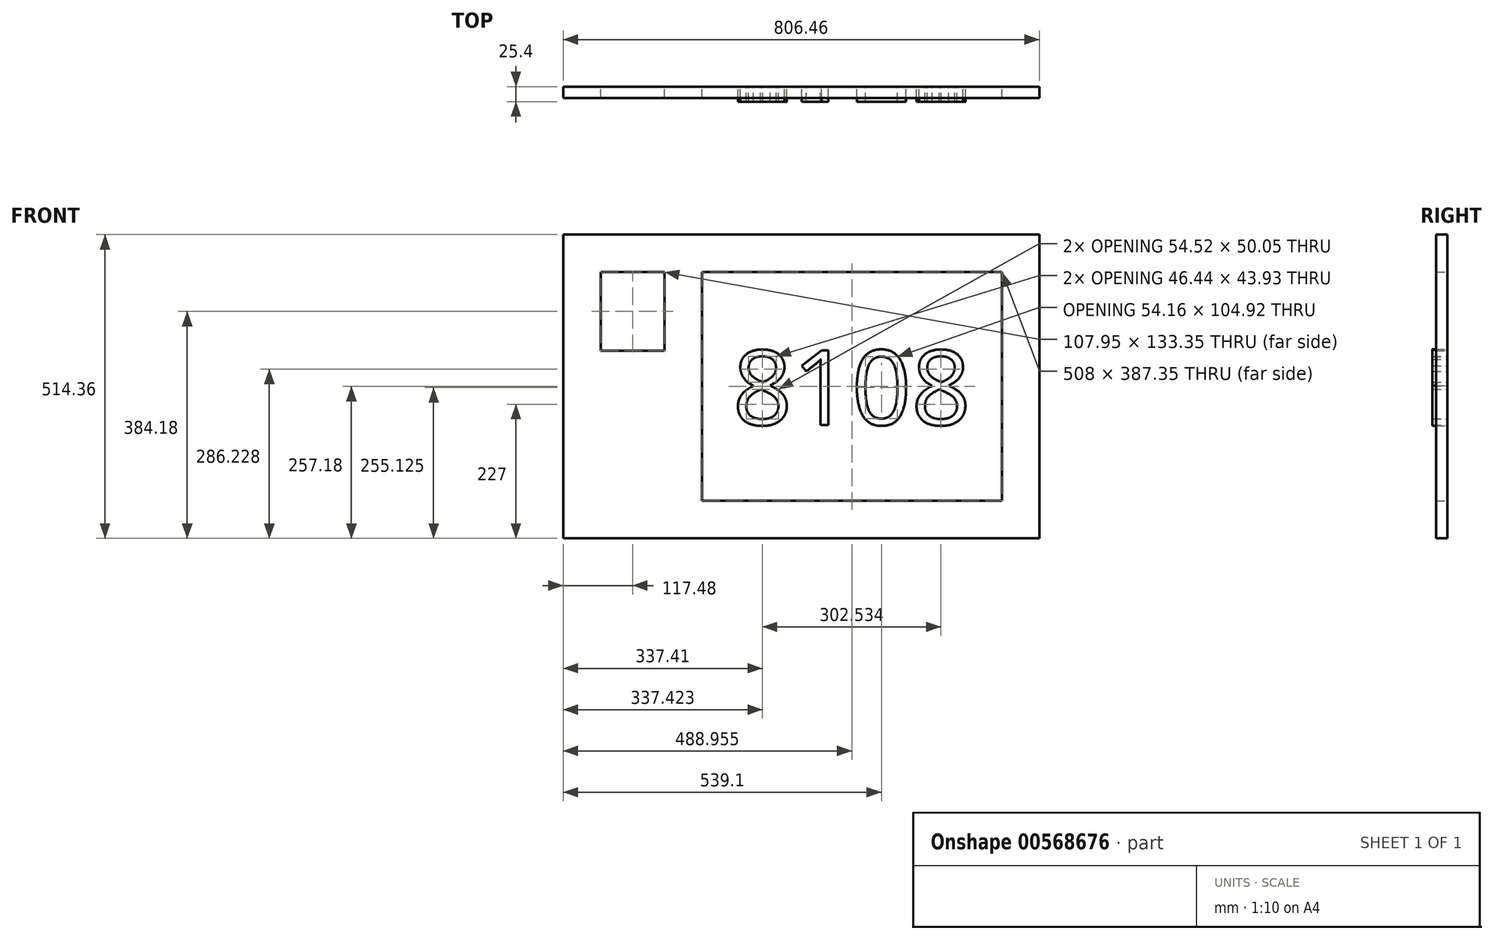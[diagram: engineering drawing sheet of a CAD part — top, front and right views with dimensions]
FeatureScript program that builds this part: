
annotation { "Feature Type Name" : "Feature", "Feature Type Description" : "" }
export const myFeature = defineFeature(function(context is Context, id is Id, definition is map)
    precondition{}
    {
        {
            var Q0;
            Q0=qCreatedBy(makeId("Front.planeOp"),FACE);
            var sketch = newSketch(context, id + "F0", { "sketchPlane" : qUnion([Q0])});
            skLineSegment(sketch, "E0.bottom", {"start": v(339.73, 193.68) * mm, "end": v(-339.73, 193.67) * mm});
            skLineSegment(sketch, "E0.top", {"start": v(339.73, -193.67) * mm, "end": v(-339.73, -193.68) * mm});
            skLineSegment(sketch, "E0.left", {"start": v(339.73, 193.68) * mm, "end": v(339.73, -193.67) * mm});
            skLineSegment(sketch, "E0.right", {"start": v(-339.73, 193.67) * mm, "end": v(-339.73, -193.68) * mm});
            skPoint(sketch, "E0.middle", {"position": v(0, 0) * mm});
            skLineSegment(sketch, "E1.0", {"start": v(403.23, 257.18) * mm, "end": v(403.23, -257.17) * mm});
            skLineSegment(sketch, "E1.1", {"start": v(403.23, 257.18) * mm, "end": v(-403.23, 257.17) * mm});
            skLineSegment(sketch, "E1.2", {"start": v(-403.23, 257.17) * mm, "end": v(-403.23, -257.18) * mm});
            skLineSegment(sketch, "E1.3", {"start": v(403.23, -257.17) * mm, "end": v(-403.23, -257.18) * mm});
            skLineSegment(sketch, "E2", {"start": v(-403.23, 257.17) * mm, "end": v(-339.73, 193.67) * mm});
            skLineSegment(sketch, "E3", {"start": v(403.23, 257.18) * mm, "end": v(339.73, 193.68) * mm});
            skLineSegment(sketch, "E4", {"start": v(339.73, -193.67) * mm, "end": v(403.23, -257.17) * mm});
            skLineSegment(sketch, "E5", {"start": v(-339.73, -193.68) * mm, "end": v(-403.23, -257.18) * mm});
            skLineSegment(sketch, "E6", {"start": v(-231.78, 193.67) * mm, "end": v(-231.77, -193.68) * mm});
            skLineSegment(sketch, "E7", {"start": v(-168.28, 193.67) * mm, "end": v(-168.28, -193.68) * mm});
            skLineSegment(sketch, "E8", {"start": v(-339.73, -3.18) * mm, "end": v(-231.78, -3.18) * mm});
            skLineSegment(sketch, "E9", {"start": v(-339.73, -130.18) * mm, "end": v(-231.77, -130.18) * mm});
            skLineSegment(sketch, "E10", {"start": v(-339.73, 60.32) * mm, "end": v(-231.78, 60.32) * mm});
            skText(sketch, "E11", { "text": "8108", "fontName": "OpenSans-Regular.ttf"});
            skLineSegment(sketch, "E12", {"start": v(-339.73, -66.68) * mm, "end": v(-231.78, -66.67) * mm});
            const initialGuessF0  = {"E11": [-0.11616, -0.0651, 1, 0, 0.127]};
            skSetInitialGuess(sketch, initialGuessF0);
            skSolve(sketch);
        }
        {
            var Q0;
            Q0=makeQuery(id+"F0.imprint","IMPRINT",FACE,{"disambiguationData":[TD([[makeQuery(id+"F0.imprint","IMPRINT",EDGE,{"derivedFrom":sQuery(id+"F0.wireOp",EDGE,"E1.2")}),1.0]])]});
            var Q1;
            Q1=makeQuery(id+"F0.imprint","IMPRINT",FACE,{"disambiguationData":[TD([[makeQuery(id+"F0.imprint","IMPRINT",EDGE,{"derivedFrom":sQuery(id+"F0.wireOp",EDGE,"E1.1")}),1.0]])]});
            var Q2;
            Q2=makeQuery(id+"F0.imprint","IMPRINT",FACE,{"disambiguationData":[TD([[makeQuery(id+"F0.imprint","IMPRINT",EDGE,{"derivedFrom":sQuery(id+"F0.wireOp",EDGE,"E0.left")}),1.0]])]});
            var Q3;
            Q3=makeQuery(id+"F0.imprint","IMPRINT",FACE,{"disambiguationData":[TD([[makeQuery(id+"F0.imprint","IMPRINT",EDGE,{"derivedFrom":sQuery(id+"F0.wireOp",EDGE,"E1.3")}),-1.0]])]});
            var Q4;
            {var subQ6=sQuery(id+"F0.wireOp",EDGE,"E7");Q4=makeQuery(id+"F0.imprint","IMPRINT",FACE,{"disambiguationData":[TD([[makeQuery(id+"F0.imprint","IMPRINT",EDGE,{"derivedFrom":subQ6}),-1.0]])]});}
            var Q5;
            {var subQ5=sQuery(id+"F0.wireOp",EDGE,"E9");Q5=makeQuery(id+"F0.imprint","IMPRINT",FACE,{"disambiguationData":[TD([[makeQuery(id+"F0.imprint","IMPRINT",EDGE,{"derivedFrom":subQ5}),-1.0]])]});}
            var Q6;
            {var subQ0=sQuery(id+"F0.wireOp",EDGE,"AUJ6MDYE-TVH4-ssOK-fysN-27W06VGnZsak");Q6=makeQuery(id+"F0.imprint","IMPRINT",FACE,{"disambiguationData":[TD([[makeQuery(id+"F0.imprint","IMPRINT",EDGE,{"derivedFrom":subQ0}),-1.0]])]});}
            var Q7;
            {var subQ0=sQuery(id+"F0.wireOp",EDGE,"E8");Q7=makeQuery(id+"F0.imprint","IMPRINT",FACE,{"disambiguationData":[TD([[makeQuery(id+"F0.imprint","IMPRINT",EDGE,{"derivedFrom":subQ0}),-1.0]])]});}
            var Q8;
            {var subQ0=sQuery(id+"F0.wireOp",EDGE,"E8");Q8=makeQuery(id+"F0.imprint","IMPRINT",FACE,{"disambiguationData":[TD([[makeQuery(id+"F0.imprint","IMPRINT",EDGE,{"derivedFrom":subQ0}),1.0]])]});}
            extrude(context, id + "F1", {"entities" : qUnion([Q0, Q1, Q2, Q3, Q4, Q5, Q6, Q7, Q8]), "depth" : 19.05 * mm, "offsetDistance" : 25.4 * mm});
        }
        {
            var Q0;
            Q0=makeQuery(id+"F0.imprint","IMPRINT",FACE,{"disambiguationData":[TD([[makeQuery(id+"F0.imprint","IMPRINT",EDGE,{"derivedFrom":sQuery(id+"F0.wireOp",EDGE,"E11.sketch_text.stroke-0")}),-1.0]])]});
            extrude(context, id + "F2", {"entities" : qUnion([Q0]), "depth" : 25.4 * mm, "offsetDistance" : 25.4 * mm});
        }
        {
            var Q0;
            Q0=makeQuery(id+"F0.imprint","IMPRINT",FACE,{"disambiguationData":[TD([[makeQuery(id+"F0.imprint","IMPRINT",EDGE,{"derivedFrom":sQuery(id+"F0.wireOp",EDGE,"E11.sketch_text.stroke-31")}),-1.0]])]});
            var Q1;
            Q1=makeQuery(id+"F0.imprint","IMPRINT",FACE,{"disambiguationData":[TD([[makeQuery(id+"F0.imprint","IMPRINT",EDGE,{"derivedFrom":sQuery(id+"F0.wireOp",EDGE,"E11.sketch_text.stroke-40")}),-1.0]])]});
            var Q2;
            Q2=makeQuery(id+"F0.imprint","IMPRINT",FACE,{"disambiguationData":[TD([[makeQuery(id+"F0.imprint","IMPRINT",EDGE,{"derivedFrom":sQuery(id+"F0.wireOp",EDGE,"E11.sketch_text.stroke-56")}),-1.0]])]});
            extrude(context, id + "F3", {"entities" : qUnion([Q0, Q1, Q2]), "depth" : 25.4 * mm, "offsetDistance" : 25.4 * mm});
        }
        {
            var Q0;
            {var subQ0=sQuery(id+"F0.wireOp",EDGE,"E9");Q0=makeQuery(id+"F0.imprint","IMPRINT",FACE,{"disambiguationData":[TD([[makeQuery(id+"F0.imprint","IMPRINT",EDGE,{"derivedFrom":subQ0}),1.0]])]});}
            extrude(context, id + "F4", {"entities" : qUnion([Q0]), "operationType" : NewBodyOperationType.ADD, "depth" : 19.05 * mm, "offsetDistance" : 25.4 * mm});
        }
    });
